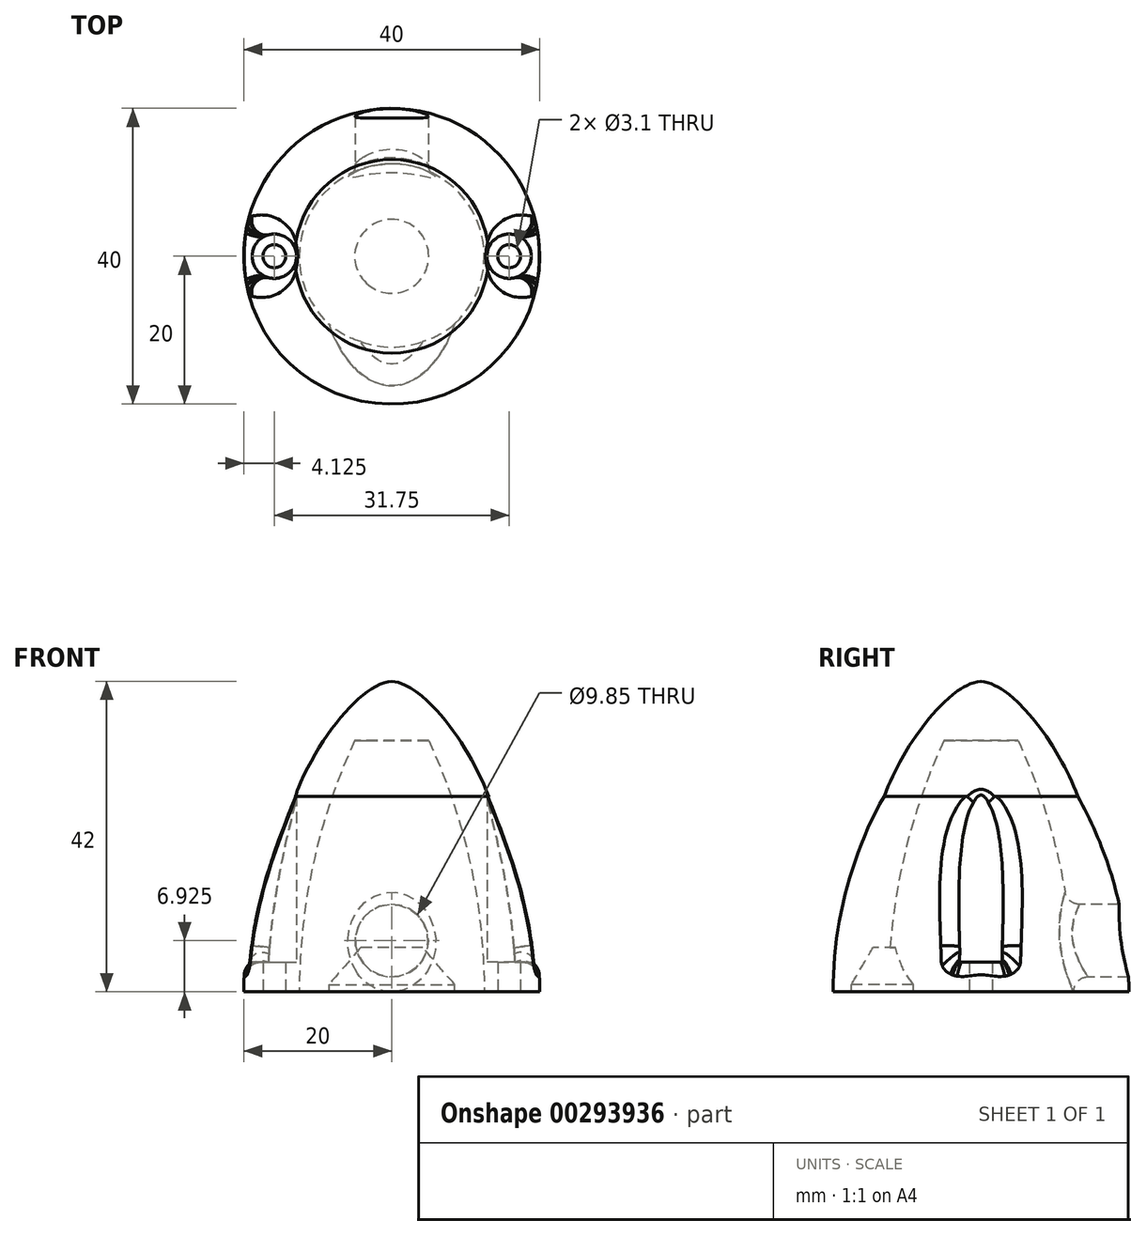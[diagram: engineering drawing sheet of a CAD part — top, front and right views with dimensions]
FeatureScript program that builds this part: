
annotation { "Feature Type Name" : "Feature", "Feature Type Description" : "" }
export const myFeature = defineFeature(function(context is Context, id is Id, definition is map)
    precondition{}
    {
        {
            var Q0;
            Q0=qCreatedBy(makeId("Front.planeOp"),FACE);
            var sketch = newSketch(context, id + "F0", { "sketchPlane" : qUnion([Q0])});
            skLineSegment(sketch, "E0", {"start": v(0, 42) * mm, "end": v(0, 0) * mm});
            skLineSegment(sketch, "E1", {"start": v(0, 0) * mm, "end": v(-20, 0) * mm});
            skArc(sketch, "E2", {"start": v(-13.1, 26.45) * mm, "mid": v(-18.25, 13.67) * mm, "end": v(-20, 0) * mm});
            skLineSegment(sketch, "E3", {"start": v(-20, 0) * mm, "end": v(-20, 34.55) * mm, "construction": true});
            skFitSpline(sketch, "E4", {"points": [v(0, 42) * mm, v(-13.1, 26.45) * mm], "startDerivative": vector(-11.82, -0.6) * mm, "endDerivative": vector(-9, -23.63) * mm});
            skSolve(sketch);
        }
        {
            var Q0;
            Q0=makeQuery(id+"F0.imprint","IMPRINT",FACE,{"disambiguationData":[TD([[makeQuery(id+"F0.imprint","IMPRINT",EDGE,{"derivedFrom":sQuery(id+"F0.wireOp",EDGE,"E0")}),-1.0]])]});
            var Q1;
            Q1=sQuery(id+"F0.wireOp",EDGE,"E0");
            revolve(context, id + "F1", {"surfaceOperationType" : NewSurfaceOperationType.NEW, "entities" : qUnion([Q0]), "axis" : qUnion([Q1]), "revolveType" : RevolveType.FULL});
        }
        {
            var Q0;
            Q0=makeQuery(id+"F1.opRevolve","SWEPT_FACE",FACE,{"disambiguationData":[OSD([sQuery(id+"F0.wireOp",EDGE,"E1")])]});
            var sketch = newSketch(context, id + "F2", { "sketchPlane" : qUnion([Q0])});
            skCircle(sketch, "E5", {"center": v(15.88, 0) * mm, "radius": 1.55 * mm});
            skCircle(sketch, "E6", {"center": v(-15.88, 0) * mm, "radius": 1.55 * mm});
            skLineSegment(sketch, "E7", {"start": v(15.88, 0) * mm, "end": v(-15.88, 0) * mm, "construction": true});
            skSolve(sketch);
        }
        {
            var Q0;
            Q0 = qSketchRegion(id + "F2", true);
            extrude(context, id + "F3", {"entities" : qUnion([Q0]), "operationType" : NewBodyOperationType.REMOVE, "endBound" : BoundingType.THROUGH_ALL, "oppositeDirection" : true, "depth" : 25 * mm, "offsetDistance" : 25 * mm});
        }
        {
            var Q0;
            Q0=qCreatedBy(makeId("Front.planeOp"),FACE);
            var sketch = newSketch(context, id + "F4", { "sketchPlane" : qUnion([Q0])});
            skLineSegment(sketch, "E8", {"start": v(-12.5, 0) * mm, "end": v(0, 0) * mm});
            skLineSegment(sketch, "E9", {"start": v(0, 0) * mm, "end": v(0, 34) * mm});
            skLineSegment(sketch, "E10", {"start": v(0, 34) * mm, "end": v(-5, 34) * mm});
            skArc(sketch, "E11", {"start": v(-5, 34) * mm, "mid": v(-10.6, 17.4) * mm, "end": v(-12.5, 0) * mm});
            skLineSegment(sketch, "E12", {"start": v(-12.5, 0) * mm, "end": v(-12.5, 20.35) * mm, "construction": true});
            skSolve(sketch);
        }
        {
            var Q0;
            Q0 = qSketchRegion(id + "F4", true);
            var Q1;
            Q1=sQuery(id+"F4.wireOp",EDGE,"E9");
            revolve(context, id + "F5", {"operationType" : NewBodyOperationType.REMOVE, "surfaceOperationType" : NewSurfaceOperationType.NEW, "entities" : qUnion([Q0]), "axis" : qUnion([Q1]), "revolveType" : RevolveType.FULL, "oppositeDirection" : true});
        }
        {
            var Q0;
            Q0=makeQuery(id+"F1.opRevolve","SWEPT_FACE",FACE,{"disambiguationData":[OSD([sQuery(id+"F0.wireOp",EDGE,"E1")])]});
            var sketch = newSketch(context, id + "F6", { "sketchPlane" : qUnion([Q0])});
            skCircle(sketch, "E13", {"center": v(-15.88, 0) * mm, "radius": 3 * mm});
            skCircle(sketch, "E14", {"center": v(15.88, 0) * mm, "radius": 3 * mm});
            skSolve(sketch);
        }
        {
            var Q0;
            Q0 = qSketchRegion(id + "F6", true);
            extrude(context, id + "F7", {"entities" : qUnion([Q0]), "operationType" : NewBodyOperationType.REMOVE, "endBound" : BoundingType.THROUGH_ALL, "oppositeDirection" : true, "depth" : 25 * mm, "offsetDistance" : 25 * mm, "hasSecondDirection" : true, "secondDirectionOppositeDirection" : true, "secondDirectionDepth" : 4 * mm});
        }
        {
            var Q0;
            Q0=makeQuery(id+"F7.boolean.opBoolean","INTERSECT",EDGE,{"derivedFrom":[makeQuery(id+"F1.opRevolve","SWEPT_FACE",FACE,{"disambiguationData":[OSD([sQuery(id+"F0.wireOp",EDGE,"E2")])]}),makeQuery(id+"F7.opExtrude","SWEPT_FACE",FACE,{"disambiguationData":[OSD([sQuery(id+"F6.wireOp",EDGE,"E13")])]})]});
            var Q1;
            Q1=makeQuery(id+"F7.boolean.opBoolean","INTERSECT",EDGE,{"derivedFrom":[makeQuery(id+"F1.opRevolve","SWEPT_FACE",FACE,{"disambiguationData":[OSD([sQuery(id+"F0.wireOp",EDGE,"E4")])]}),makeQuery(id+"F7.opExtrude","SWEPT_FACE",FACE,{"disambiguationData":[OSD([sQuery(id+"F6.wireOp",EDGE,"E13")])]})]});
            var Q2;
            Q2=makeQuery(id+"F7.boolean.opBoolean","INTERSECT",EDGE,{"derivedFrom":[makeQuery(id+"F1.opRevolve","SWEPT_FACE",FACE,{"disambiguationData":[OSD([sQuery(id+"F0.wireOp",EDGE,"E2")])]}),makeQuery(id+"F7.opExtrude","SWEPT_FACE",FACE,{"disambiguationData":[OSD([sQuery(id+"F6.wireOp",EDGE,"E14")])]})]});
            var Q3;
            Q3=makeQuery(id+"F7.boolean.opBoolean","INTERSECT",EDGE,{"derivedFrom":[makeQuery(id+"F1.opRevolve","SWEPT_FACE",FACE,{"disambiguationData":[OSD([sQuery(id+"F0.wireOp",EDGE,"E4")])]}),makeQuery(id+"F7.opExtrude","SWEPT_FACE",FACE,{"disambiguationData":[OSD([sQuery(id+"F6.wireOp",EDGE,"E14")])]})]});
            fillet(context, id + "F8", {"entities" : qUnion([Q0, Q1, Q2, Q3]), "radius" : 2 * mm, "tangentPropagation" : true, "allowEdgeOverflow" : false});
        }
        {
            var Q0;
            Q0=qCreatedBy(makeId("Front.planeOp"),FACE);
            var sketch = newSketch(context, id + "F9", { "sketchPlane" : qUnion([Q0])});
            skCircle(sketch, "E15", {"center": v(0, 6.92) * mm, "radius": 4.92 * mm});
            skSolve(sketch);
        }
        {
            var Q0;
            Q0 = qSketchRegion(id + "F9", true);
            extrude(context, id + "F10", {"entities" : qUnion([Q0]), "operationType" : NewBodyOperationType.REMOVE, "oppositeDirection" : true, "depth" : 25 * mm, "offsetDistance" : 25 * mm});
        }
        {
            var Q0;
            Q0=makeQuery(id+"F1.opRevolve","SWEPT_FACE",FACE,{"disambiguationData":[OSD([sQuery(id+"F0.wireOp",EDGE,"E1")])]});
            var sketch = newSketch(context, id + "F11", { "sketchPlane" : qUnion([Q0])});
            skEllipticalArc(sketch, "E16", {});
            skLineSegment(sketch, "E17", {"start": v(10, 0) * mm, "end": v(-10, 0) * mm});
            const initialGuessF11  = {"E16": [0, 0, 0, 1, 0.0175, 0.01, 4.71238898038469, 1.5707963267948966]};
            skSetInitialGuess(sketch, initialGuessF11);
            skSolve(sketch);
        }
        {
            var Q0;
            Q0 = qSketchRegion(id + "F11", true);
            extrude(context, id + "F12", {"entities" : qUnion([Q0]), "operationType" : NewBodyOperationType.REMOVE, "oppositeDirection" : true, "depth" : 6 * mm, "offsetDistance" : 25 * mm});
        }
        {
            var Q0;
            {var subQ0=sQuery(id+"F11.wireOp",EDGE,"E16");Q0=makeQuery(id+"F12.boolean.opBoolean","COPY",EDGE,{"disambiguationData":[TD([makeQuery(id+"F5.boolean.opBoolean","COPY",FACE,{"derivedFrom":makeQuery(id+"F5.opRevolve","SWEPT_FACE",FACE,{"disambiguationData":[OSD([sQuery(id+"F4.wireOp",EDGE,"E11")])]})}),makeQuery(id+"F12.opExtrude","SWEPT_FACE",FACE,{"disambiguationData":[OSD([subQ0])]}),makeQuery(id+"F12.opExtrude","CAP_FACE",FACE,{"disambiguationData":[OSD([subQ0])],"isStart":false})])],"derivedFrom":makeQuery(id+"F12.opExtrude","CAP_EDGE",EDGE,{"disambiguationData":[OSD([subQ0])],"isStart":false})});}
            chamfer(context, id + "F13", {"entities" : qUnion([Q0]), "chamferType" : ChamferType.OFFSET_ANGLE, "width" : 5 * mm, "oppositeDirection" : true, "angle" : 30 * degree, "tangentPropagation" : true});
        }
        {
            var Q0;
            Q0=makeQuery(id+"F10.boolean.opBoolean","INTERSECT",EDGE,{"derivedFrom":[makeQuery(id+"F5.boolean.opBoolean","COPY",FACE,{"derivedFrom":makeQuery(id+"F5.opRevolve","SWEPT_FACE",FACE,{"disambiguationData":[OSD([sQuery(id+"F4.wireOp",EDGE,"E11")])]})}),makeQuery(id+"F10.opExtrude","SWEPT_FACE",FACE,{"disambiguationData":[OSD([sQuery(id+"F9.wireOp",EDGE,"E15")])]})]});
            fillet(context, id + "F14", {"entities" : qUnion([Q0]), "radius" : 2 * mm, "tangentPropagation" : true, "allowEdgeOverflow" : false});
        }
    });
